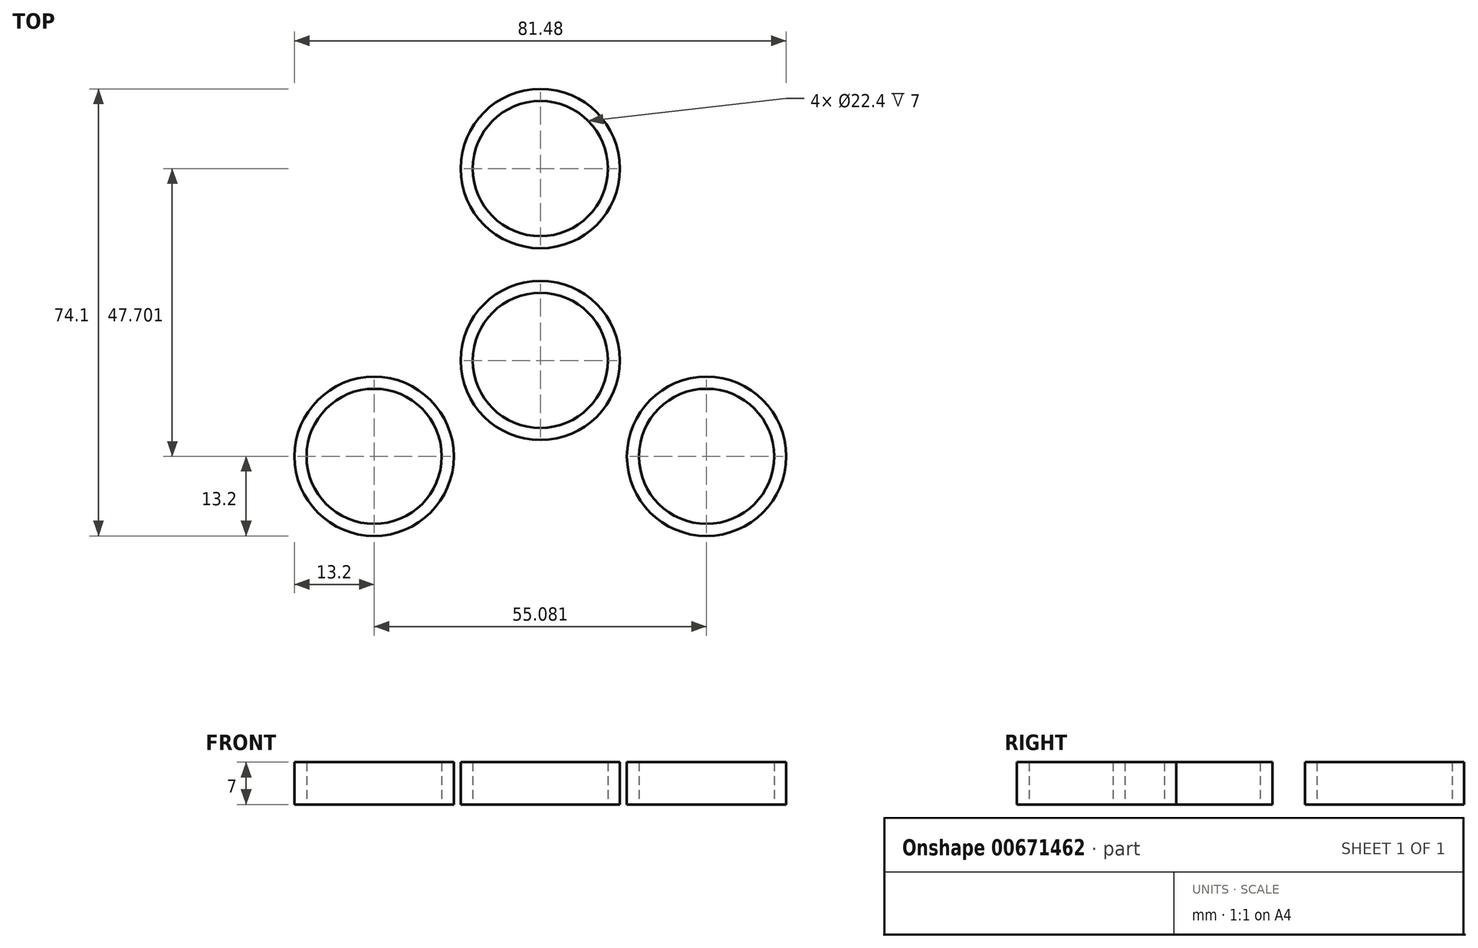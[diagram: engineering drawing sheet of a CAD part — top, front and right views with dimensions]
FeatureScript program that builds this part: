
annotation { "Feature Type Name" : "Feature", "Feature Type Description" : "" }
export const myFeature = defineFeature(function(context is Context, id is Id, definition is map)
    precondition{}
    {
        {
            var Q0;
            Q0=qCreatedBy(makeId("Top.planeOp"),FACE);
            var sketch = newSketch(context, id + "F0", { "sketchPlane" : qUnion([Q0])});
            skCircle(sketch, "E0", {"center": v(0, 0) * mm, "radius": 11.2 * mm});
            skCircle(sketch, "E1", {"center": v(0, 0) * mm, "radius": 13.2 * mm});
            skCircle(sketch, "E2", {"center": v(0, 31.8) * mm, "radius": 11.2 * mm});
            skCircle(sketch, "E3", {"center": v(0, 31.8) * mm, "radius": 13.2 * mm});
            skCircle(sketch, "E4.1.0", {"center": v(-27.54, -15.9) * mm, "radius": 13.2 * mm});
            skCircle(sketch, "E4.1.1", {"center": v(-27.54, -15.9) * mm, "radius": 11.2 * mm});
            skCircle(sketch, "E4.2.0", {"center": v(27.54, -15.9) * mm, "radius": 13.2 * mm});
            skCircle(sketch, "E4.2.1", {"center": v(27.54, -15.9) * mm, "radius": 11.2 * mm});
            skSolve(sketch);
        }
        {
            var Q0;
            Q0=qCreatedBy(makeId("Top.planeOp"),FACE);
            var sketch = newSketch(context, id + "F1", { "sketchPlane" : qUnion([Q0])});
            skArc(sketch, "E5", {"start": v(-22.28, -3.88) * mm, "mid": v(-11.09, 6.95) * mm, "end": v(-9.17, 22.4) * mm});
            skArc(sketch, "E6.1.0", {"start": v(14.5, -17.35) * mm, "mid": v(-0.47, -13.08) * mm, "end": v(-14.8, -19.14) * mm});
            skArc(sketch, "E6.2.0", {"start": v(7.78, 21.23) * mm, "mid": v(11.56, 6.13) * mm, "end": v(23.98, -3.26) * mm});
            skPoint(sketch, "E6.center", {"position": v(0, 0) * mm});
            skSolve(sketch);
        }
        {
            var Q0;
            Q0=makeQuery(id+"F0.imprint","IMPRINT",FACE,{"disambiguationData":[TD([[makeQuery(id+"F0.imprint","IMPRINT",EDGE,{"derivedFrom":sQuery(id+"F0.wireOp",EDGE,"E2")}),-1.0]])]});
            var Q1;
            Q1=makeQuery(id+"F0.imprint","IMPRINT",FACE,{"disambiguationData":[TD([[makeQuery(id+"F0.imprint","IMPRINT",EDGE,{"derivedFrom":sQuery(id+"F0.wireOp",EDGE,"E4.2.0")}),1.0]])]});
            var Q2;
            Q2=makeQuery(id+"F0.imprint","IMPRINT",FACE,{"disambiguationData":[TD([[makeQuery(id+"F0.imprint","IMPRINT",EDGE,{"derivedFrom":sQuery(id+"F0.wireOp",EDGE,"E0")}),-1.0]])]});
            var Q3;
            Q3=makeQuery(id+"F0.imprint","IMPRINT",FACE,{"disambiguationData":[TD([[makeQuery(id+"F0.imprint","IMPRINT",EDGE,{"derivedFrom":sQuery(id+"F0.wireOp",EDGE,"E4.1.0")}),1.0]])]});
            extrude(context, id + "F2", {"entities" : qUnion([Q0, Q1, Q2, Q3]), "depth" : 7 * mm, "offsetDistance" : 25 * mm});
        }
        {
            var Q0;
            Q0=sQuery(id+"F1.wireOp",EDGE,"E5");
            var Q1;
            Q1=sQuery(id+"F1.wireOp",EDGE,"E6.2.0");
            var Q2;
            Q2=sQuery(id+"F1.wireOp",EDGE,"E6.1.0");
            extrude(context, id + "F3", {"bodyType" : ToolBodyType.SURFACE, "surfaceEntities" : qUnion([Q0, Q1, Q2]), "depth" : 7 * mm, "offsetDistance" : 25 * mm});
        }
    });
